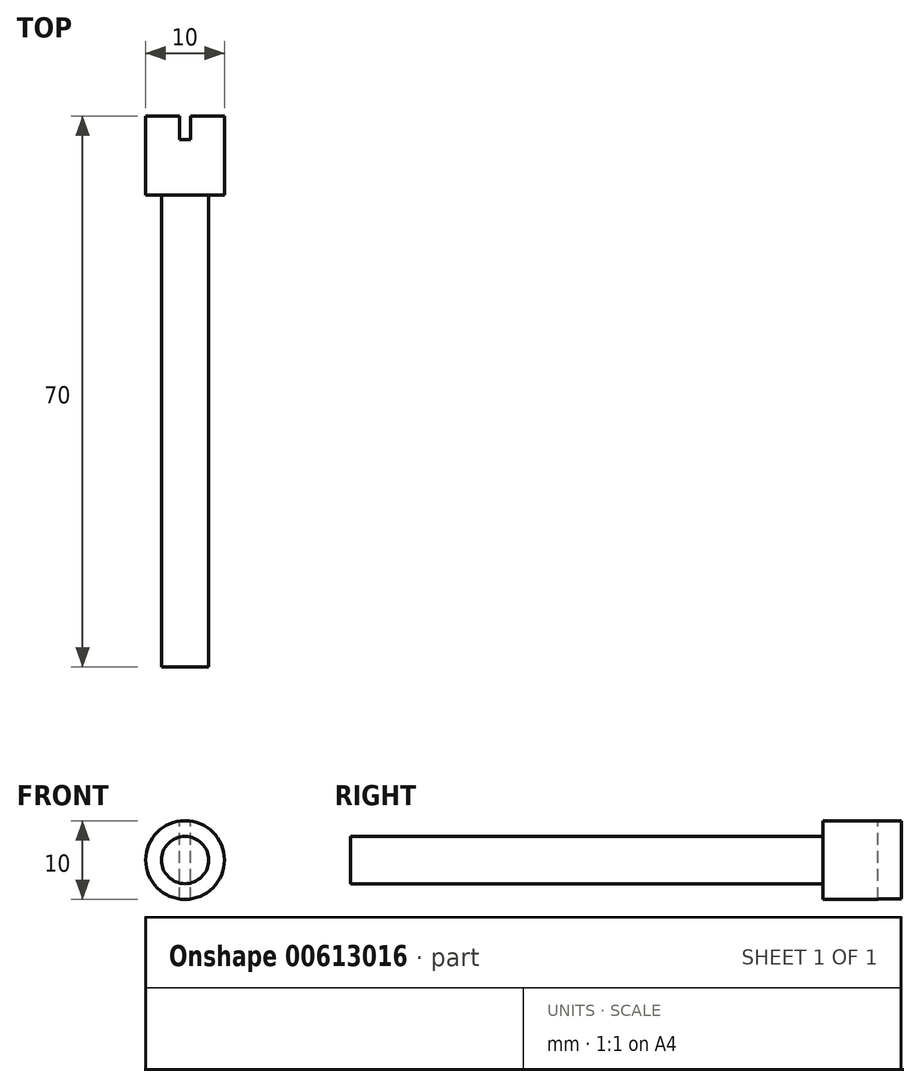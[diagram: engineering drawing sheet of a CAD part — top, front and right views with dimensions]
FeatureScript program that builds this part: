
annotation { "Feature Type Name" : "Feature", "Feature Type Description" : "" }
export const myFeature = defineFeature(function(context is Context, id is Id, definition is map)
    precondition{}
    {
        {
            var Q0;
            Q0=qCreatedBy(makeId("Front.planeOp"),FACE);
            var sketch = newSketch(context, id + "F0", { "sketchPlane" : qUnion([Q0])});
            skCircle(sketch, "E0", {"center": v(0, 0) * mm, "radius": 3 * mm});
            skSolve(sketch);
        }
        {
            var Q0;
            Q0 = qSketchRegion(id + "F0", true);
            extrude(context, id + "F1", {"entities" : qUnion([Q0]), "depth" : 60 * mm, "offsetDistance" : 25 * mm});
        }
        {
            var Q0;
            Q0=qCreatedBy(makeId("Front.planeOp"),FACE);
            var sketch = newSketch(context, id + "F2", { "sketchPlane" : qUnion([Q0])});
            skCircle(sketch, "E1", {"center": v(0, 0) * mm, "radius": 5 * mm});
            skSolve(sketch);
        }
        {
            var Q0;
            Q0 = qSketchRegion(id + "F2", true);
            extrude(context, id + "F3", {"entities" : qUnion([Q0]), "operationType" : NewBodyOperationType.ADD, "oppositeDirection" : true, "depth" : 10 * mm, "offsetDistance" : 25 * mm});
        }
        {
            var Q0;
            Q0=makeQuery(id+"F3.opExtrude","CAP_FACE",FACE,{"disambiguationData":[OSD([sQuery(id+"F2.wireOp",EDGE,"E1")])],"isStart":false});
            var sketch = newSketch(context, id + "F4", { "sketchPlane" : qUnion([Q0])});
            skLineSegment(sketch, "E2.bottom", {"start": v(0.69, -5) * mm, "end": v(-0.69, -5) * mm});
            skLineSegment(sketch, "E2.top", {"start": v(0.69, 5) * mm, "end": v(-0.69, 5) * mm});
            skLineSegment(sketch, "E2.left", {"start": v(0.69, -5) * mm, "end": v(0.69, 5) * mm});
            skLineSegment(sketch, "E2.right", {"start": v(-0.69, -5) * mm, "end": v(-0.69, 5) * mm});
            skPoint(sketch, "E2.middle", {"position": v(0, 0) * mm});
            skSolve(sketch);
        }
        {
            var Q0;
            Q0 = qSketchRegion(id + "F4", true);
            extrude(context, id + "F5", {"entities" : qUnion([Q0]), "operationType" : NewBodyOperationType.REMOVE, "oppositeDirection" : true, "depth" : 3 * mm, "offsetDistance" : 25 * mm});
        }
    });
